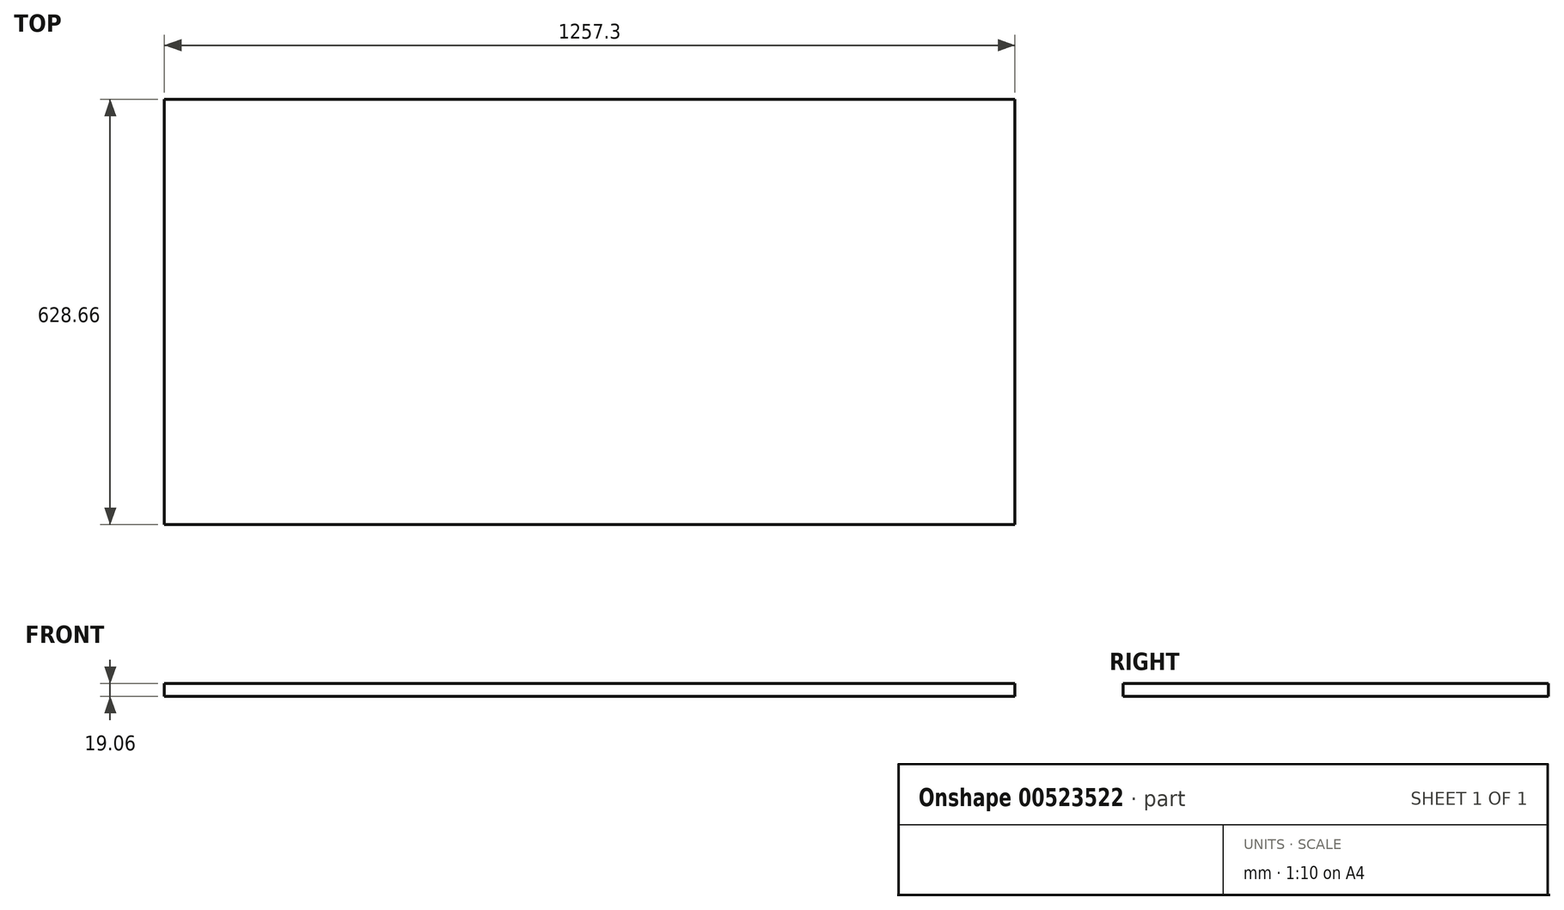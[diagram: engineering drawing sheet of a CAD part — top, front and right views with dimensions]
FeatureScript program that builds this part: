
annotation { "Feature Type Name" : "Feature", "Feature Type Description" : "" }
export const myFeature = defineFeature(function(context is Context, id is Id, definition is map)
    precondition{}
    {
        {
            var Q0;
            Q0=qCreatedBy(makeId("Top.planeOp"),FACE);
            var sketch = newSketch(context, id + "F0", { "sketchPlane" : qUnion([Q0])});
            skLineSegment(sketch, "E0.bottom", {"start": v(-628.65, 314.33) * mm, "end": v(628.65, 314.33) * mm});
            skLineSegment(sketch, "E0.top", {"start": v(-628.65, -314.33) * mm, "end": v(628.65, -314.33) * mm});
            skLineSegment(sketch, "E0.left", {"start": v(-628.65, 314.33) * mm, "end": v(-628.65, -314.33) * mm});
            skLineSegment(sketch, "E0.right", {"start": v(628.65, 314.33) * mm, "end": v(628.65, -314.33) * mm});
            skPoint(sketch, "E0.middle", {"position": v(0, 0) * mm});
            skSolve(sketch);
        }
        {
            var Q0;
            Q0=makeQuery(id+"F0.imprint","IMPRINT",FACE,{"disambiguationData":[TD([[makeQuery(id+"F0.imprint","IMPRINT",EDGE,{"derivedFrom":sQuery(id+"F0.wireOp",EDGE,"E0.bottom")}),-1.0]])]});
            extrude(context, id + "F1", {"entities" : qUnion([Q0]), "endBound" : BoundingType.SYMMETRIC, "depth" : 19.05 * mm, "offsetDistance" : 25.4 * mm});
        }
    });
